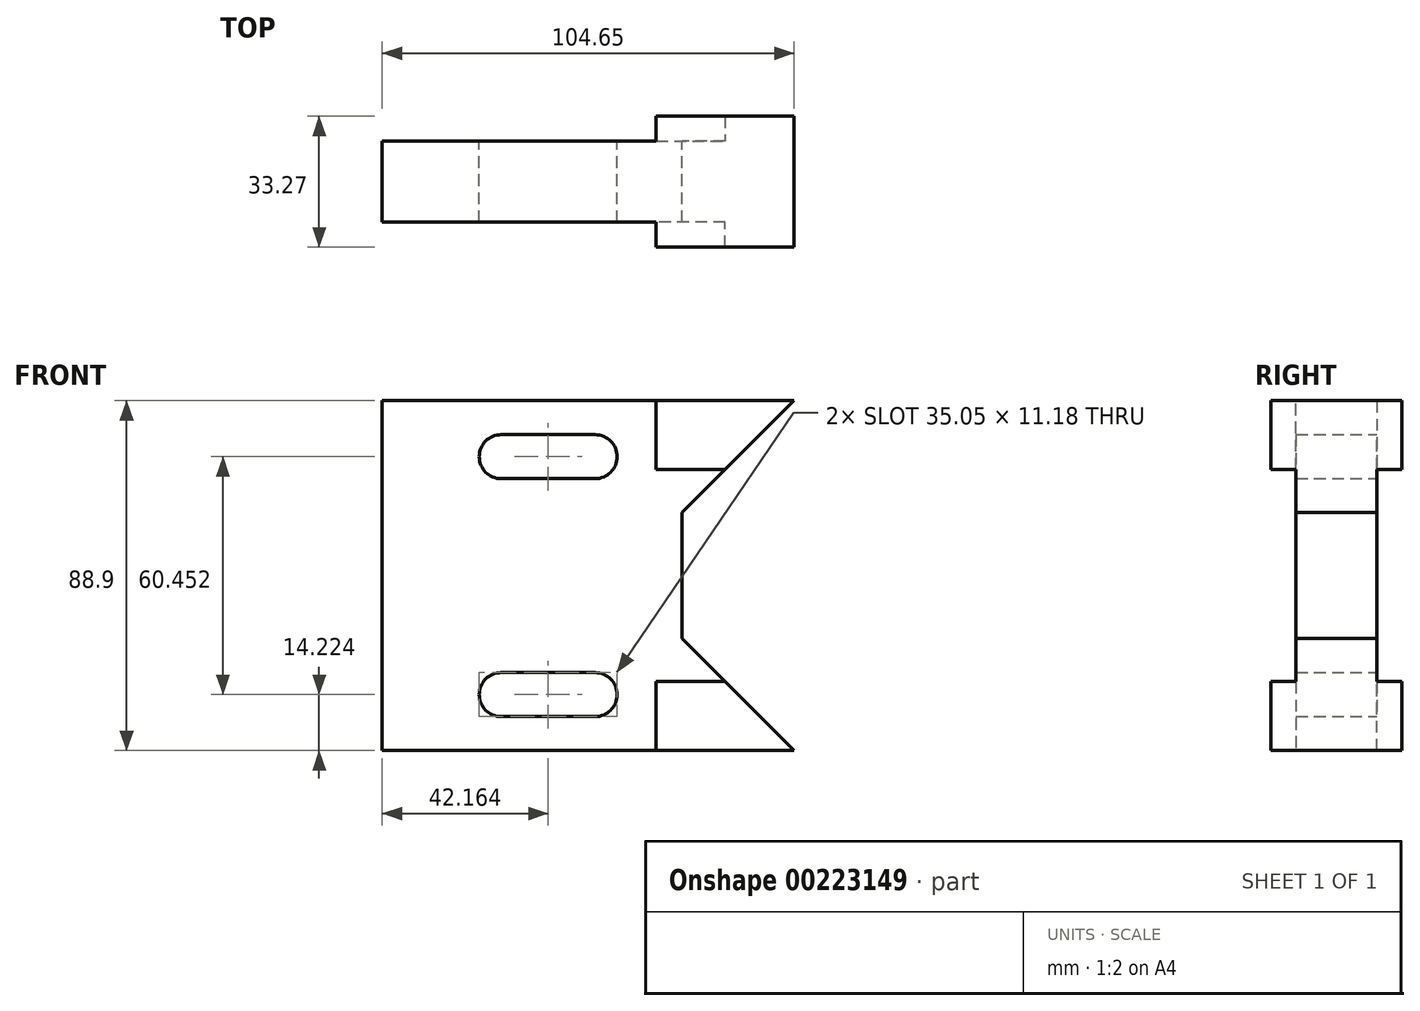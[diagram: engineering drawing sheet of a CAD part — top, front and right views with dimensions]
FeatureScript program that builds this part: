
annotation { "Feature Type Name" : "Feature", "Feature Type Description" : "" }
export const myFeature = defineFeature(function(context is Context, id is Id, definition is map)
    precondition{}
    {
        {
            var Q0;
            Q0=qCreatedBy(makeId("Front.planeOp"),FACE);
            var sketch = newSketch(context, id + "F0", { "sketchPlane" : qUnion([Q0])});
            skLineSegment(sketch, "E0", {"start": v(0, 0) * mm, "end": v(104.65, 0) * mm});
            skLineSegment(sketch, "E1", {"start": v(30.23, 19.81) * mm, "end": v(54.1, 19.81) * mm});
            skLineSegment(sketch, "E2", {"start": v(30.23, 8.64) * mm, "end": v(54.1, 8.64) * mm});
            skArc(sketch, "E3", {"start": v(30.23, 19.81) * mm, "mid": v(24.64, 14.22) * mm, "end": v(30.23, 8.64) * mm});
            skArc(sketch, "E4", {"start": v(54.1, 8.64) * mm, "mid": v(59.69, 14.22) * mm, "end": v(54.1, 19.81) * mm});
            skLineSegment(sketch, "E5", {"start": v(0, 0) * mm, "end": v(0, 44.45) * mm});
            skLineSegment(sketch, "E6", {"start": v(104.65, 0) * mm, "end": v(76.2, 28.45) * mm});
            skLineSegment(sketch, "E7", {"start": v(0, 28.45) * mm, "end": v(76.2, 28.45) * mm});
            skLineSegment(sketch, "E8", {"start": v(0, 44.45) * mm, "end": v(76.2, 44.45) * mm});
            skLineSegment(sketch, "E9", {"start": v(76.2, 44.45) * mm, "end": v(76.2, 28.45) * mm});
            skLineSegment(sketch, "E10.MirrorCS", {"start": v(76.2, 44.45) * mm, "end": v(76.2, 60.45) * mm});
            skLineSegment(sketch, "E11.MirrorCS", {"start": v(30.23, 69.09) * mm, "end": v(54.1, 69.09) * mm});
            skArc(sketch, "E12.MirrorCS", {"start": v(54.1, 80.26) * mm, "mid": v(59.69, 74.68) * mm, "end": v(54.1, 69.09) * mm});
            skLineSegment(sketch, "E13.MirrorCS", {"start": v(0, 88.9) * mm, "end": v(0, 44.45) * mm});
            skLineSegment(sketch, "E14.MirrorCS", {"start": v(0, 88.9) * mm, "end": v(104.65, 88.9) * mm});
            skArc(sketch, "E15.MirrorCS", {"start": v(30.23, 69.09) * mm, "mid": v(24.64, 74.68) * mm, "end": v(30.23, 80.26) * mm});
            skLineSegment(sketch, "E16.MirrorCS", {"start": v(30.23, 80.26) * mm, "end": v(54.1, 80.26) * mm});
            skLineSegment(sketch, "E17.MirrorCS", {"start": v(0, 60.45) * mm, "end": v(76.2, 60.45) * mm});
            skLineSegment(sketch, "E18.MirrorCS", {"start": v(104.65, 88.9) * mm, "end": v(76.2, 60.45) * mm});
            skSolve(sketch);
        }
        {
            var Q0;
            Q0 = qSketchRegion(id + "F0", true);
            extrude(context, id + "F1", {"entities" : qUnion([Q0]), "depth" : 20.57 * mm});
        }
        {
            var Q0;
            Q0=makeQuery(id+"F1.opExtrude","CAP_FACE",FACE,{"disambiguationData":[OSD([sQuery(id+"F0.wireOp",EDGE,"E0"),sQuery(id+"F0.wireOp",EDGE,"E1"),sQuery(id+"F0.wireOp",EDGE,"E2"),sQuery(id+"F0.wireOp",EDGE,"E3"),sQuery(id+"F0.wireOp",EDGE,"E4"),sQuery(id+"F0.wireOp",EDGE,"E5"),sQuery(id+"F0.wireOp",EDGE,"E6"),sQuery(id+"F0.wireOp",EDGE,"E7")])],"isStart":false});
            var sketch = newSketch(context, id + "F2", { "sketchPlane" : qUnion([Q0])});
            skLineSegment(sketch, "E19", {"start": v(69.6, 0) * mm, "end": v(69.6, 17.53) * mm});
            skLineSegment(sketch, "E20", {"start": v(69.6, 17.53) * mm, "end": v(87.12, 17.53) * mm});
            skLineSegment(sketch, "E21.MirrorCS", {"start": v(69.6, 71.37) * mm, "end": v(87.12, 71.37) * mm});
            skLineSegment(sketch, "E22.MirrorCS", {"start": v(69.6, 88.9) * mm, "end": v(69.6, 71.37) * mm});
            skLineSegment(sketch, "E23", {"start": v(69.6, 88.9) * mm, "end": v(104.65, 88.9) * mm});
            skLineSegment(sketch, "E24", {"start": v(104.65, 88.9) * mm, "end": v(87.12, 71.37) * mm});
            skLineSegment(sketch, "E25", {"start": v(87.12, 17.53) * mm, "end": v(104.65, 0) * mm});
            skLineSegment(sketch, "E26", {"start": v(104.65, 0) * mm, "end": v(69.6, 0) * mm});
            skSolve(sketch);
        }
        {
            var Q0;
            Q0 = qSketchRegion(id + "F0", true);
            extrude(context, id + "F3", {"entities" : qUnion([Q0]), "operationType" : NewBodyOperationType.ADD, "depth" : 20.57 * mm});
        }
        {
            var Q0;
            Q0 = qSketchRegion(id + "F2", true);
            extrude(context, id + "F4", {"entities" : qUnion([Q0]), "operationType" : NewBodyOperationType.ADD, "endBound" : BoundingType.SYMMETRIC, "depth" : 12.7 * mm});
        }
        {
            var Q0;
            Q0=makeQuery(id+"F4.opExtrude","CAP_FACE",FACE,{"disambiguationData":[OSD([sQuery(id+"F2.wireOp",EDGE,"E19"),sQuery(id+"F2.wireOp",EDGE,"E20"),sQuery(id+"F2.wireOp",EDGE,"E25"),sQuery(id+"F2.wireOp",EDGE,"E26")])],"isStart":false});
            var sketch = newSketch(context, id + "F5", { "sketchPlane" : qUnion([Q0])});
            skLineSegment(sketch, "E27", {"start": v(69.6, 17.53) * mm, "end": v(87.12, 17.53) * mm});
            skLineSegment(sketch, "E28", {"start": v(87.12, 17.53) * mm, "end": v(104.65, 0) * mm});
            skLineSegment(sketch, "E29", {"start": v(104.65, 0) * mm, "end": v(69.6, 0) * mm});
            skLineSegment(sketch, "E30", {"start": v(69.6, 0) * mm, "end": v(69.6, 17.53) * mm});
            skSolve(sketch);
        }
        {
            var Q0;
            Q0 = qSketchRegion(id + "F5", true);
            extrude(context, id + "F6", {"entities" : qUnion([Q0]), "operationType" : NewBodyOperationType.ADD, "oppositeDirection" : true, "depth" : 33.27 * mm});
        }
        {
            var Q0;
            Q0=makeQuery(id+"F4.opExtrude","CAP_FACE",FACE,{"disambiguationData":[OSD([sQuery(id+"F2.wireOp",EDGE,"E21.MirrorCS"),sQuery(id+"F2.wireOp",EDGE,"E22.MirrorCS"),sQuery(id+"F2.wireOp",EDGE,"E23"),sQuery(id+"F2.wireOp",EDGE,"E24")])],"isStart":false});
            var sketch = newSketch(context, id + "F7", { "sketchPlane" : qUnion([Q0])});
            skLineSegment(sketch, "E31", {"start": v(69.6, 88.9) * mm, "end": v(69.6, 71.37) * mm});
            skLineSegment(sketch, "E32", {"start": v(69.6, 71.37) * mm, "end": v(87.12, 71.37) * mm});
            skLineSegment(sketch, "E33", {"start": v(87.12, 71.37) * mm, "end": v(104.65, 88.9) * mm});
            skLineSegment(sketch, "E34", {"start": v(104.65, 88.9) * mm, "end": v(69.6, 88.9) * mm});
            skSolve(sketch);
        }
        {
            var Q0;
            Q0 = qSketchRegion(id + "F7", true);
            extrude(context, id + "F8", {"entities" : qUnion([Q0]), "operationType" : NewBodyOperationType.ADD, "oppositeDirection" : true, "depth" : 33.27 * mm});
        }
    });
